# Revit family: wd-120_220bzr5_50Hz
name_source: partatom
category: 機械設備
units: mm (PartAtom-declared; Revit-internal decimal feet)

## family parameters
OmniClass タイトル = Centrifugal Fans
OmniClass 番号 = 23.75.35.17.27
パーツ タイプ = 標準
ロード時にボイドで切り取り = いいえ
丸型コネクタ寸法 = 直径を使用
作業面ベース = いいえ
共有 = いいえ
常に垂直 = はい
部屋計算ポイント = はい

## types (2) — shared parameters
D1 = 352  [stored 1.15486 ft]
Depth = 280
H1 = 38
Height = 195  [stored 0.639764 ft]
IfcExportAs = IfcFanType
IfcExportType = PROPELLORAXIAL
MAX静圧 = 0.0 Pa
MID静圧 = 0.0 Pa
MID風量 = 0.0 m³/h
MIN静圧 = 0.0 Pa
OmniClassCode = 23-33 31 19 11 15
URL = https://www.mitsubishielectric.co.jp
Uniclass2015Code = Pr_65_67_29_12
Uniclass2015Title = Centrifugal fans
Uniclass2015Version = Systems v1.9
W1 = 472
Width = 400
カバーマテリアル = 合成樹脂(白)
マテリアル = 亜鉛メッキ鋼板
仕様書バージョン = Version1.0
企業コード = 108420
分類コード = 50052503100080
周波数 = 50 Hz
本体固定用穴ピッチ1 = 265
本体固定用穴ピッチ2 = 304
本体固定用穴ピッチ3 = 424  [stored 1.39108 ft]
本体固定用穴ピッチ4 = 224  [stored 0.734908 ft]
法定耐用年数 = 10
点検口 = はい
点検口_Depth = 450  [stored 1.47638 ft]
点検口離隔 = 150
相 = 1
積算_科目 = 2 換気設備
製品リリース年月 = 2022年6月1日
製品出荷対象 = 国内
製造元 = 三菱電機株式会社
設置方法 = カセット形
説明 = バス乾燥・暖房・換気システム 浴室暖房機〈換気扇連動形〉
負荷分類 = 3_ファン類
運転質量 = 0.00 kg
電動機出力 = 0 W

## per-type parameters (varying)
| type | MAX風量 | MIN風量 | 価格 | 極数 | 消費電力 | 製品質量 | 質量 | 電圧 |
| WD-120BZR5 | 165.0 m³/h | 120.0 m³/h | 108800 $ | 2 | 1300 W | 6.50 kg | 7.80 kg | 100 V |
| WD-220BZR5 | 210.0 m³/h | 110.0 m³/h | 137100 $ | 3 | 2300 W | 7.00 kg | 8.40 kg | 200 V |

note: column(s) folded — value = type name in every type: モデル

note: [stored X ft] marks values corroborated as IEEE doubles in the binary element streams (Revit-internal decimal feet)
